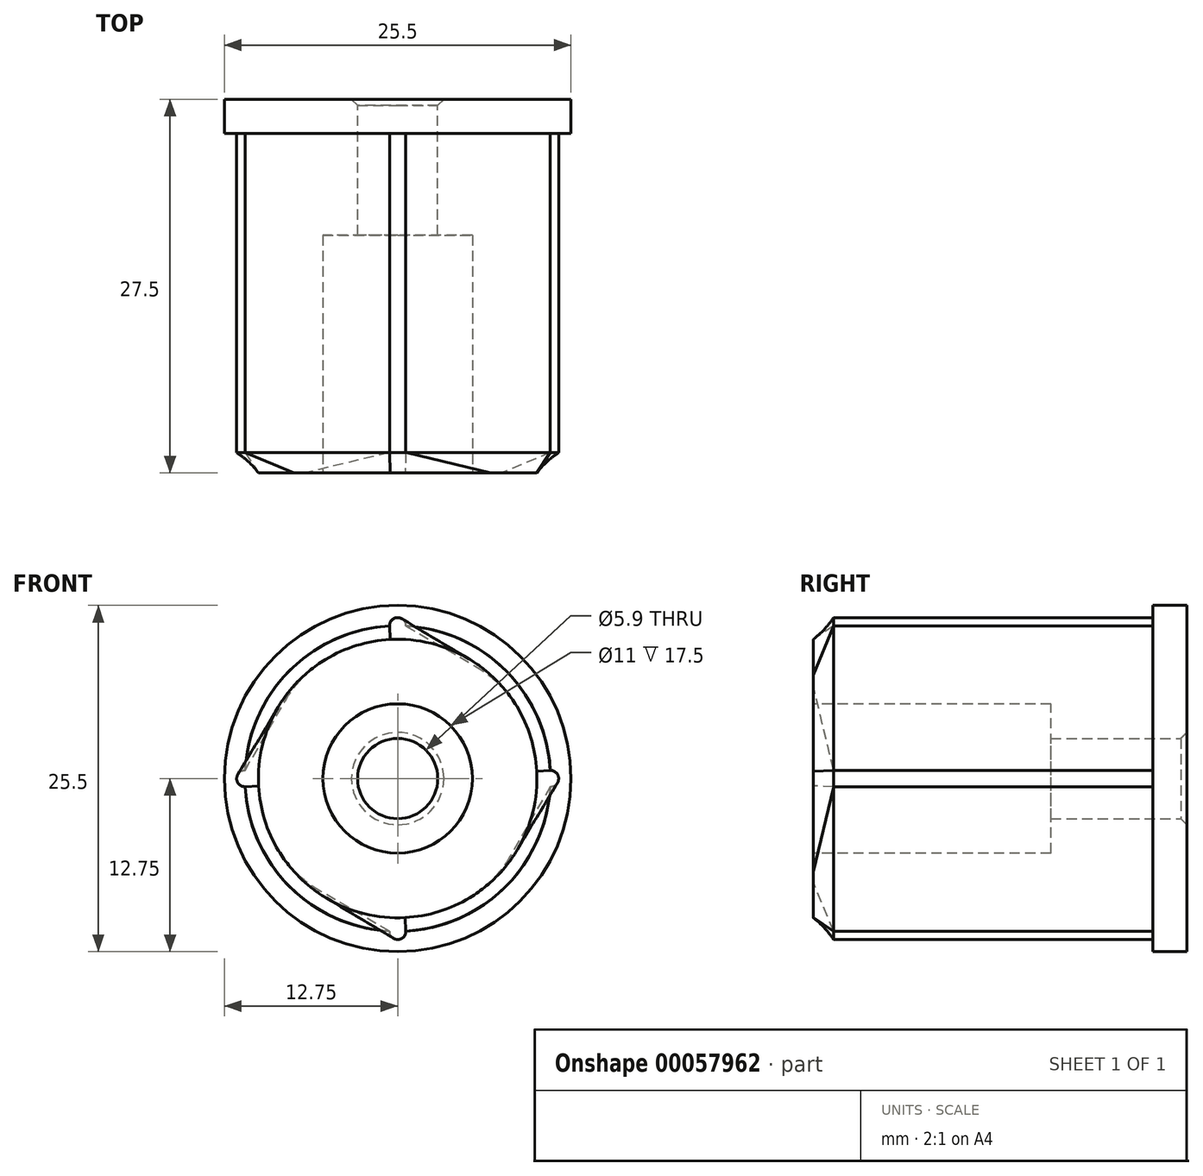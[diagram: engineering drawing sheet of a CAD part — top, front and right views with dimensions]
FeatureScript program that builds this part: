
annotation { "Feature Type Name" : "Feature", "Feature Type Description" : "" }
export const myFeature = defineFeature(function(context is Context, id is Id, definition is map)
    precondition{}
    {
        {
            var Q0;
            Q0=qCreatedBy(makeId("Front.planeOp"),FACE);
            var sketch = newSketch(context, id + "F0", { "sketchPlane" : qUnion([Q0])});
            skArc(sketch, "E0", {"start": v(-0.6, 11.23) * mm, "mid": v(-7.95, 7.95) * mm, "end": v(-11.23, 0.6) * mm});
            skArc(sketch, "E1", {"start": v(0.6, 11.23) * mm, "mid": v(0, 11.85) * mm, "end": v(-0.6, 11.23) * mm});
            skArc(sketch, "E2", {"start": v(11.23, -0.6) * mm, "mid": v(11.85, 0) * mm, "end": v(11.23, 0.6) * mm});
            skArc(sketch, "E3", {"start": v(-0.6, -11.23) * mm, "mid": v(0, -11.85) * mm, "end": v(0.6, -11.23) * mm});
            skArc(sketch, "E4", {"start": v(-11.23, 0.6) * mm, "mid": v(-11.85, 0) * mm, "end": v(-11.23, -0.6) * mm});
            skArc(sketch, "E5.trimOffspring", {"start": v(11.23, 0.6) * mm, "mid": v(7.95, 7.95) * mm, "end": v(0.6, 11.23) * mm});
            skArc(sketch, "E6.trimOffspring", {"start": v(-11.23, -0.6) * mm, "mid": v(-7.95, -7.95) * mm, "end": v(-0.6, -11.23) * mm});
            skArc(sketch, "E7.trimOffspring", {"start": v(0.6, -11.23) * mm, "mid": v(7.95, -7.95) * mm, "end": v(11.23, -0.6) * mm});
            skSolve(sketch);
        }
        {
            var Q0;
            Q0 = qSketchRegion(id + "F0", true);
            extrude(context, id + "F1", {"entities" : qUnion([Q0]), "depth" : 23.5 * mm});
        }
        {
            var Q0;
            Q0=makeQuery(id+"F1.opExtrude","CAP_FACE",FACE,{"disambiguationData":[OSD([sQuery(id+"F0.wireOp",EDGE,"E0"),sQuery(id+"F0.wireOp",EDGE,"E1"),sQuery(id+"F0.wireOp",EDGE,"E2"),sQuery(id+"F0.wireOp",EDGE,"E3"),sQuery(id+"F0.wireOp",EDGE,"E4"),sQuery(id+"F0.wireOp",EDGE,"E5.trimOffspring"),sQuery(id+"F0.wireOp",EDGE,"E6.trimOffspring"),sQuery(id+"F0.wireOp",EDGE,"E7.trimOffspring")])],"isStart":false});
            cPlane(context, id + "F2", {"entities" : qUnion([Q0]), "cplaneType" : CPlaneType.OFFSET, "offset" : 1.5 * mm, "width" : 150 * mm, "height" : 150 * mm});
        }
        {
            var Q0;
            Q0=qCreatedBy(id+"F2.planeOp",FACE);
            var sketch = newSketch(context, id + "F3", { "sketchPlane" : qUnion([Q0])});
            skCircle(sketch, "E8", {"center": v(0, 0) * mm, "radius": 10.25 * mm});
            skSolve(sketch);
        }
        {
            var Q0;
            Q0=makeQuery(id+"F1.opExtrude","CAP_FACE",FACE,{"disambiguationData":[OSD([sQuery(id+"F0.wireOp",EDGE,"E0"),sQuery(id+"F0.wireOp",EDGE,"E1"),sQuery(id+"F0.wireOp",EDGE,"E2"),sQuery(id+"F0.wireOp",EDGE,"E3"),sQuery(id+"F0.wireOp",EDGE,"E4"),sQuery(id+"F0.wireOp",EDGE,"E5.trimOffspring"),sQuery(id+"F0.wireOp",EDGE,"E6.trimOffspring"),sQuery(id+"F0.wireOp",EDGE,"E7.trimOffspring")])],"isStart":false});
            var Q1;
            Q1=makeQuery(id+"F3.imprint","IMPRINT",FACE,{"disambiguationData":[TD([[makeQuery(id+"F3.imprint","IMPRINT",EDGE,{"derivedFrom":sQuery(id+"F3.wireOp",EDGE,"E8")}),1.0]])]});
            loft(context, id + "F4", {"operationType" : NewBodyOperationType.ADD, "sheetProfilesArray" : [{ "sheetProfileEntities" : qUnion([Q0]) }, { "sheetProfileEntities" : qUnion([Q1]) }]});
        }
        {
            var Q0;
            Q0=makeQuery(id+"F1.opExtrude","CAP_FACE",FACE,{"disambiguationData":[OSD([sQuery(id+"F0.wireOp",EDGE,"E0"),sQuery(id+"F0.wireOp",EDGE,"E1"),sQuery(id+"F0.wireOp",EDGE,"E2"),sQuery(id+"F0.wireOp",EDGE,"E3"),sQuery(id+"F0.wireOp",EDGE,"E4"),sQuery(id+"F0.wireOp",EDGE,"E5.trimOffspring"),sQuery(id+"F0.wireOp",EDGE,"E6.trimOffspring"),sQuery(id+"F0.wireOp",EDGE,"E7.trimOffspring")])],"isStart":true});
            var sketch = newSketch(context, id + "F5", { "sketchPlane" : qUnion([Q0])});
            skCircle(sketch, "E9", {"center": v(0, 0) * mm, "radius": 12.75 * mm});
            skSolve(sketch);
        }
        {
            var Q0;
            Q0 = qSketchRegion(id + "F5", true);
            extrude(context, id + "F6", {"entities" : qUnion([Q0]), "operationType" : NewBodyOperationType.ADD, "depth" : 2.5 * mm});
        }
        {
            var Q0;
            Q0=makeQuery(id+"F6.opExtrude","CAP_FACE",FACE,{"disambiguationData":[OSD([sQuery(id+"F5.wireOp",EDGE,"E9")])],"isStart":false});
            var sketch = newSketch(context, id + "F7", { "sketchPlane" : qUnion([Q0])});
            skPoint(sketch, "E10", {"position": v(0, 0) * mm});
            skSolve(sketch);
        }
        {
            var Q0;
            Q0=sQuery(id+"F7.wireOp",VERTEX,"E10");
            var Q1;
            Q1=makeQuery(id+"F1.opExtrude","SWEPT_BODY",BODY,{"disambiguationData":[OSD([sQuery(id+"F0.wireOp",EDGE,"E0"),sQuery(id+"F0.wireOp",EDGE,"E1"),sQuery(id+"F0.wireOp",EDGE,"E2"),sQuery(id+"F0.wireOp",EDGE,"E3"),sQuery(id+"F0.wireOp",EDGE,"E4"),sQuery(id+"F0.wireOp",EDGE,"E5.trimOffspring"),sQuery(id+"F0.wireOp",EDGE,"E6.trimOffspring"),sQuery(id+"F0.wireOp",EDGE,"E7.trimOffspring")])]});
            hole(context, id + "F8", {"style" : HoleStyle.C_SINK, "holeDiameter" : 5.9 * mm, "cSinkDiameter" : 6.8 * mm, "endStyle" : HoleEndStyle.THROUGH, "locations" : qUnion([Q0]), "scope" : qUnion([Q1]), "cSinkAngle" : 90 * degree});
        }
        {
            var Q0;
            Q0=makeQuery(id+"F4.opLoft","CAP_FACE",FACE,{"disambiguationData":[OSD([makeQuery(id+"F3.imprint","IMPRINT",FACE,{"disambiguationData":[TD([[makeQuery(id+"F3.imprint","IMPRINT",EDGE,{"derivedFrom":sQuery(id+"F3.wireOp",EDGE,"E8")}),1.0]])]})])],"isStart":true});
            var sketch = newSketch(context, id + "F9", { "sketchPlane" : qUnion([Q0])});
            skCircle(sketch, "E11", {"center": v(0, 0) * mm, "radius": 5.5 * mm});
            skSolve(sketch);
        }
        {
            var Q0;
            Q0 = qSketchRegion(id + "F9", true);
            extrude(context, id + "F10", {"entities" : qUnion([Q0]), "operationType" : NewBodyOperationType.REMOVE, "oppositeDirection" : true, "depth" : 17.5 * mm});
        }
    });
